# Revit family: Patch panel
name_source: partatom
category: Equipement spécialisé
units: mm (PartAtom-declared; Revit-internal decimal feet)

## family parameters
Basée sur le plan de construction = Non
Cote de connecteur circulaire = Utiliser le diamètre
Couper avec des vides une fois chargée = Non
Partagée = Oui
Point de calcul de pièce = Non
Toujours verticalement = Oui
Type d'élément = Normal

## types (1)
- Patch panel
    BIM wording = Patch panel 24 RJ45 Cat 5e 6 6A Keystone to equip with metal cable ring
    Cable nature for connection = Flexible
    Color = IDS_NOIR
    Connector type = RJ45
    Depth = 140 mm  [stored 0.459318 ft]
    E-catalogue link = https://www.legrand.fr
    EAN = 3414972185509
    ETIM class = EC001128
    Elévation par défaut = 0 mm  [stored 0 ft]
    Function = Patch panels connectors copper
    Height = 43.8 mm  [stored 0.143701 ft]
    IK = IK04
    Legrand part number = 632850
    Modular spacing = 19 inches
    Number of connectors = 24
    Number of height units = 1
    Operating temperature = -10_à_60
    RAL Number = 9017
    Shielded = Oui
    Storage temperature = -10_à_70
    Width (mm) = 482.6 mm

note: [stored X ft] marks values corroborated as IEEE doubles in the binary element streams (Revit-internal decimal feet)
